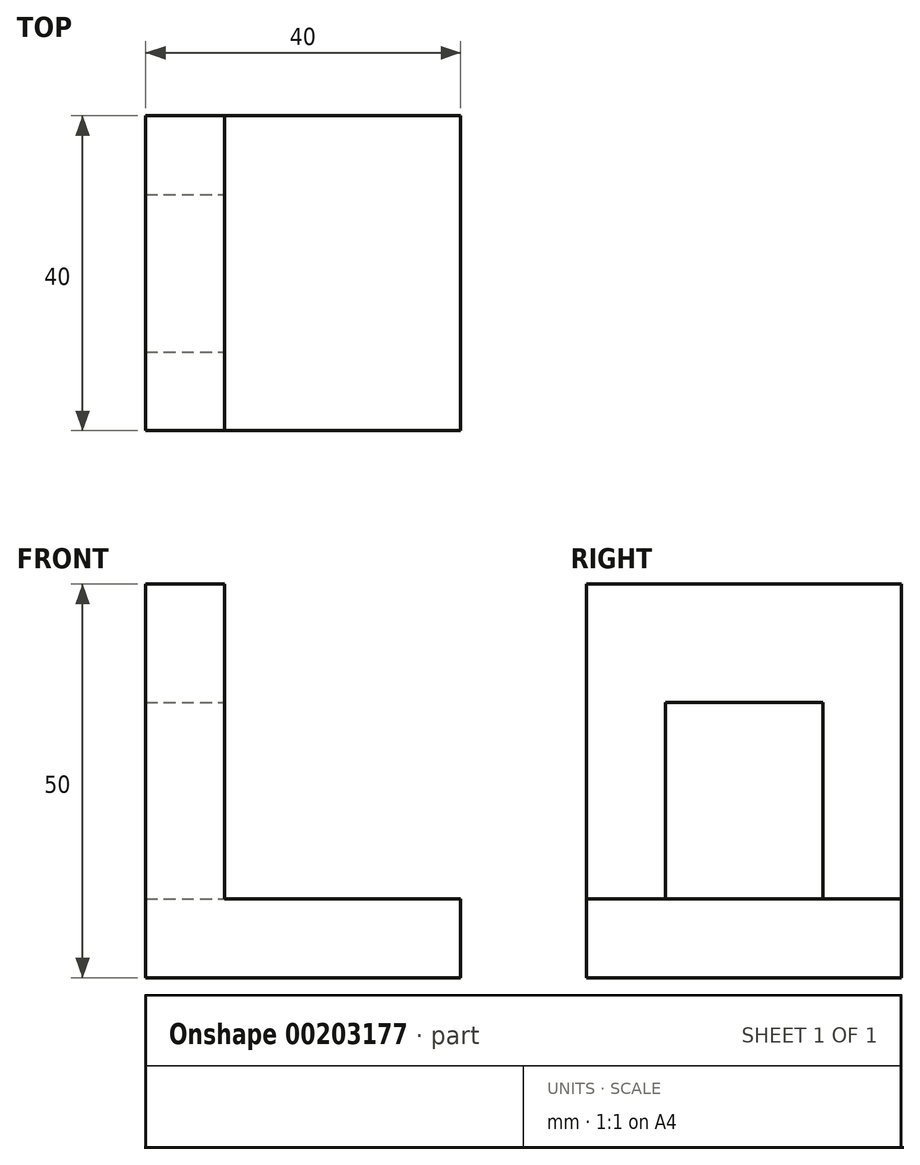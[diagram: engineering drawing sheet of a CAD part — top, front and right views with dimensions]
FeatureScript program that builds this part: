
annotation { "Feature Type Name" : "Feature", "Feature Type Description" : "" }
export const myFeature = defineFeature(function(context is Context, id is Id, definition is map)
    precondition{}
    {
        {
            var Q0;
            Q0=qCreatedBy(makeId("Front.planeOp"),FACE);
            var sketch = newSketch(context, id + "F0", { "sketchPlane" : qUnion([Q0])});
            skLineSegment(sketch, "E0", {"start": v(0, 10) * mm, "end": v(0, 0) * mm});
            skLineSegment(sketch, "E1", {"start": v(0, 0) * mm, "end": v(-40, 0) * mm});
            skLineSegment(sketch, "E2", {"start": v(-40, 0) * mm, "end": v(-40, 50) * mm});
            skLineSegment(sketch, "E3", {"start": v(-40, 50) * mm, "end": v(-30, 50) * mm});
            skLineSegment(sketch, "E4", {"start": v(-30, 50) * mm, "end": v(-30, 10) * mm});
            skLineSegment(sketch, "E5", {"start": v(-30, 10) * mm, "end": v(0, 10) * mm});
            skSolve(sketch);
        }
        {
            var Q0;
            Q0=makeQuery(id+"F0.imprint","IMPRINT",FACE,{"disambiguationData":[TD([[makeQuery(id+"F0.imprint","IMPRINT",EDGE,{"derivedFrom":sQuery(id+"F0.wireOp",EDGE,"E0")}),-1.0]])]});
            extrude(context, id + "F1", {"entities" : qUnion([Q0]), "depth" : 40 * mm, "symmetric" : true});
        }
        {
            var Q0;
            Q0=makeQuery(id+"F1.opExtrude","SWEPT_FACE",FACE,{"disambiguationData":[OSD([sQuery(id+"F0.wireOp",EDGE,"E4")])]});
            var sketch = newSketch(context, id + "F2", { "sketchPlane" : qUnion([Q0])});
            skLineSegment(sketch, "E6.bottom", {"start": v(-10, 10) * mm, "end": v(10, 10) * mm});
            skLineSegment(sketch, "E6.top", {"start": v(-10, 35) * mm, "end": v(10, 35) * mm});
            skLineSegment(sketch, "E6.left", {"start": v(-10, 10) * mm, "end": v(-10, 35) * mm});
            skLineSegment(sketch, "E6.right", {"start": v(10, 10) * mm, "end": v(10, 35) * mm});
            skSolve(sketch);
        }
        {
            var Q0;
            Q0=makeQuery(id+"F2.imprint","IMPRINT",FACE,{"disambiguationData":[TD([[makeQuery(id+"F2.imprint","IMPRINT",EDGE,{"derivedFrom":sQuery(id+"F2.wireOp",EDGE,"E6.bottom")}),1.0]])]});
            extrude(context, id + "F3", {"entities" : qUnion([Q0]), "operationType" : NewBodyOperationType.REMOVE, "oppositeDirection" : true, "depth" : 25.4 * mm});
        }
    });
